# Revit family: TYCO-FPP-FireClass-FC410DDM FIRE & GAS DET MOD
name_source: partatom
category: Electrical Fixtures
revit_build: Autodesk Revit 2014 (Build: 20130308_1515(x64)
units: mm (PartAtom-declared; Revit-internal decimal feet)

## types (1)
- TYCO-FPP-FireClass-FC410DDM FIRE & GAS DET MOD
    Description = Universal Detection Module
    EOL = 4.7KOHM
    Front cover = Yes
    Keynote = The conventional detector circuits can be configured as one Class A
circuit (loop) or two Class B spur circuits.
    Length = 60 mm
    Loop Voltage Max = 40 V DC
    Manufacturer = Tyco
    Model = FireClass-577.800.706
    Monitor Resistor Value = 100 Ohms
    Operating Temperature = - 25 - + 70 ºC
    PCB = PCB
    RT = RT
    Rear cover = Yes
    S = SS1
    Type Comments = The FC410DDM provides the ability to connect and interface 2
conventional zones, to the FireClass fire alarm controller.
    URL = https://fireclass.co.uk
    Width = 84 mm

## geometry (parser evidence)
native form markers: Sweep x6
no freeform markers — native parametric forms only
